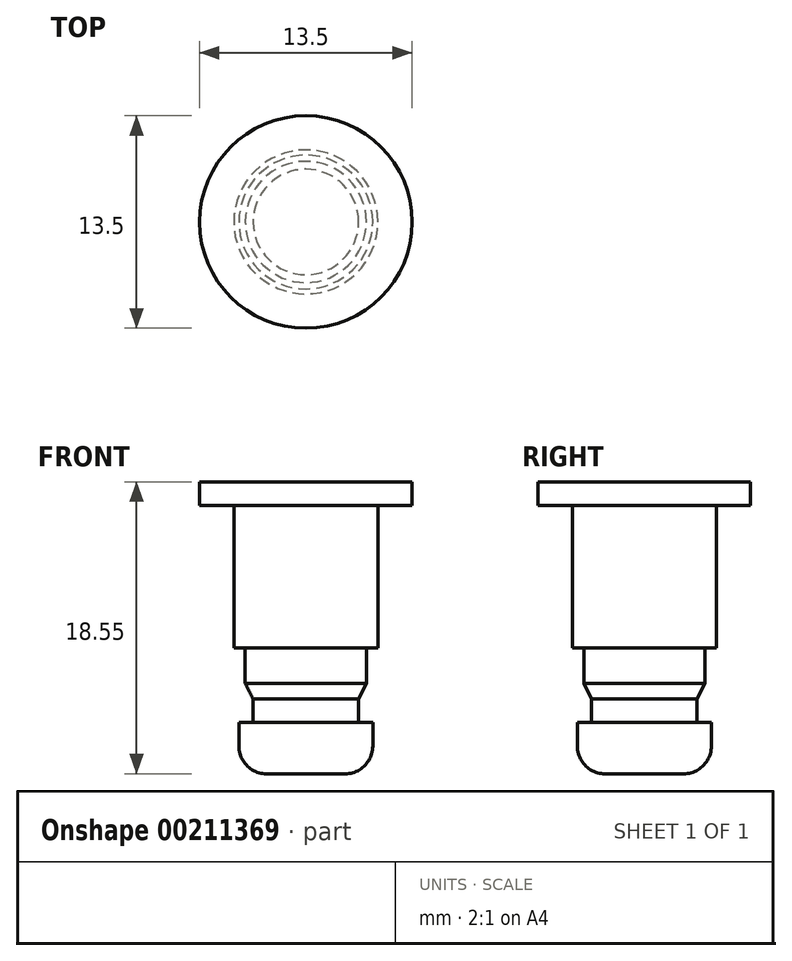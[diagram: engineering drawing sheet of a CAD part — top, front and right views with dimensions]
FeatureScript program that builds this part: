
annotation { "Feature Type Name" : "Feature", "Feature Type Description" : "" }
export const myFeature = defineFeature(function(context is Context, id is Id, definition is map)
    precondition{}
    {
        {
            var Q0;
            Q0=qCreatedBy(makeId("Top.planeOp"),FACE);
            var sketch = newSketch(context, id + "F0", { "sketchPlane" : qUnion([Q0])});
            skCircle(sketch, "E0", {"center": v(0, 0) * mm, "radius": 6.75 * mm});
            skSolve(sketch);
        }
        {
            var Q0;
            Q0 = qSketchRegion(id + "F0", true);
            extrude(context, id + "F1", {"entities" : qUnion([Q0]), "depth" : 1.5 * mm});
        }
        {
            var Q0;
            Q0=makeQuery(id+"F1.opExtrude","CAP_FACE",FACE,{"disambiguationData":[OSD([sQuery(id+"F0.wireOp",EDGE,"E0")])],"isStart":true});
            var sketch = newSketch(context, id + "F2", { "sketchPlane" : qUnion([Q0])});
            skCircle(sketch, "E1", {"center": v(0, 0) * mm, "radius": 4.58 * mm});
            skSolve(sketch);
        }
        {
            var Q0;
            Q0 = qSketchRegion(id + "F2", true);
            extrude(context, id + "F3", {"entities" : qUnion([Q0]), "operationType" : NewBodyOperationType.ADD, "depth" : 10.55 * mm - 1.5 * mm});
        }
        {
            var Q0;
            Q0=makeQuery(id+"F3.opExtrude","CAP_FACE",FACE,{"disambiguationData":[OSD([sQuery(id+"F2.wireOp",EDGE,"E1")])],"isStart":false});
            var sketch = newSketch(context, id + "F4", { "sketchPlane" : qUnion([Q0])});
            skCircle(sketch, "E2", {"center": v(0, 0) * mm, "radius": 3.85 * mm});
            skSolve(sketch);
        }
        {
            var Q0;
            Q0 = qSketchRegion(id + "F4", true);
            extrude(context, id + "F5", {"entities" : qUnion([Q0]), "operationType" : NewBodyOperationType.ADD, "depth" : 3.25 * mm});
        }
        {
            var Q0;
            Q0=makeQuery(id+"F5.opExtrude","CAP_EDGE",EDGE,{"disambiguationData":[OSD([sQuery(id+"F4.wireOp",EDGE,"E2")])],"isStart":false});
            chamfer(context, id + "F6", {"entities" : qUnion([Q0]), "chamferType" : ChamferType.TWO_OFFSETS, "width1" : .5 * mm, "oppositeDirection" : false, "width2" : 1 * mm, "tangentPropagation" : true});
        }
        {
            var Q0;
            Q0=makeQuery(id+"F5.opExtrude","CAP_FACE",FACE,{"disambiguationData":[OSD([sQuery(id+"F4.wireOp",EDGE,"E2")])],"isStart":false});
            var sketch = newSketch(context, id + "F7", { "sketchPlane" : qUnion([Q0])});
            skCircle(sketch, "E3", {"center": v(0, 0) * mm, "radius": 3.35 * mm});
            skSolve(sketch);
        }
        {
            var Q0;
            Q0 = qSketchRegion(id + "F7", true);
            extrude(context, id + "F8", {"entities" : qUnion([Q0]), "operationType" : NewBodyOperationType.ADD, "depth" : 1.5 * mm});
        }
        {
            var Q0;
            Q0=makeQuery(id+"F8.opExtrude","CAP_FACE",FACE,{"disambiguationData":[OSD([sQuery(id+"F7.wireOp",EDGE,"E3")])],"isStart":false});
            var sketch = newSketch(context, id + "F9", { "sketchPlane" : qUnion([Q0])});
            skCircle(sketch, "E4", {"center": v(0, 0) * mm, "radius": 4.25 * mm});
            skSolve(sketch);
        }
        {
            var Q0;
            Q0 = qSketchRegion(id + "F9", true);
            extrude(context, id + "F10", {"entities" : qUnion([Q0]), "operationType" : NewBodyOperationType.ADD, "depth" : 3.25 * mm});
        }
        {
            var Q0;
            Q0=makeQuery(id+"F10.opExtrude","CAP_EDGE",EDGE,{"disambiguationData":[OSD([sQuery(id+"F9.wireOp",EDGE,"E4")])],"isStart":false});
            fillet(context, id + "F11", {"entities" : qUnion([Q0]), "radius" : 1.75 * mm, "tangentPropagation" : true, "allowEdgeOverflow" : false});
        }
    });
